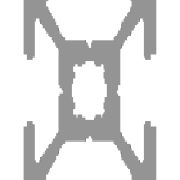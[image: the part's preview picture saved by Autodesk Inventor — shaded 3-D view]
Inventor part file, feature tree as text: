
AUTODESK INVENTOR PART (.ipt)
format: ipt  version: 2021.3 (Build 253353000, 353)  size: 286,208 bytes
history: native  units: mm
features: other x4, sketch x3, extrude x1, plane x1
ambient origin geometry x8: Origin, YZ Plane, XZ Plane, XY Plane, X Axis, Y Axis, Z Axis, Center Point
bodies: Body (feature_tree)
feature tree (9):
  other  "Driven Length"
  other  "Frame Generator"
  extrude  "Extrusion_20x20"  Depth=1.5mm
  other  "Start Plane"
  other  "End Plane"
  sketch  "Sketch"  dims[d7=3.0mm d9=1.5mm d10=0.5mm d13=0.5mm d14=0.5mm d18=3.0mm d19=3.0mm d21=0.5mm d22=0.5mm d23=0.5mm d24=2.75mm d25=1.5mm d26=10.0mm d27=10.0mm d28=3.0mm d29=3.0mm d30=5.5mm d31=1.5mm d32=0.5mm d33=0.5mm d34=0.5mm d35=0.5mm d36=0.5mm d37=0.5mm d38=0.5mm d39=0.5mm d40=0.5mm d41=2.75mm d42=2.75mm d43=0.5mm d44=40.0mm d46=360.0deg d50=-0.0mm d51=660.0mm d52=0.13mm d53=0.0mm d54=90.0deg d55=660.0mm]
  sketch  "Sketch2"  dims[d4=5.5mm d5=1.5mm]
  plane  "Work Plane3"
  sketch  "Sketch3"  dims[d6=1.5mm]
